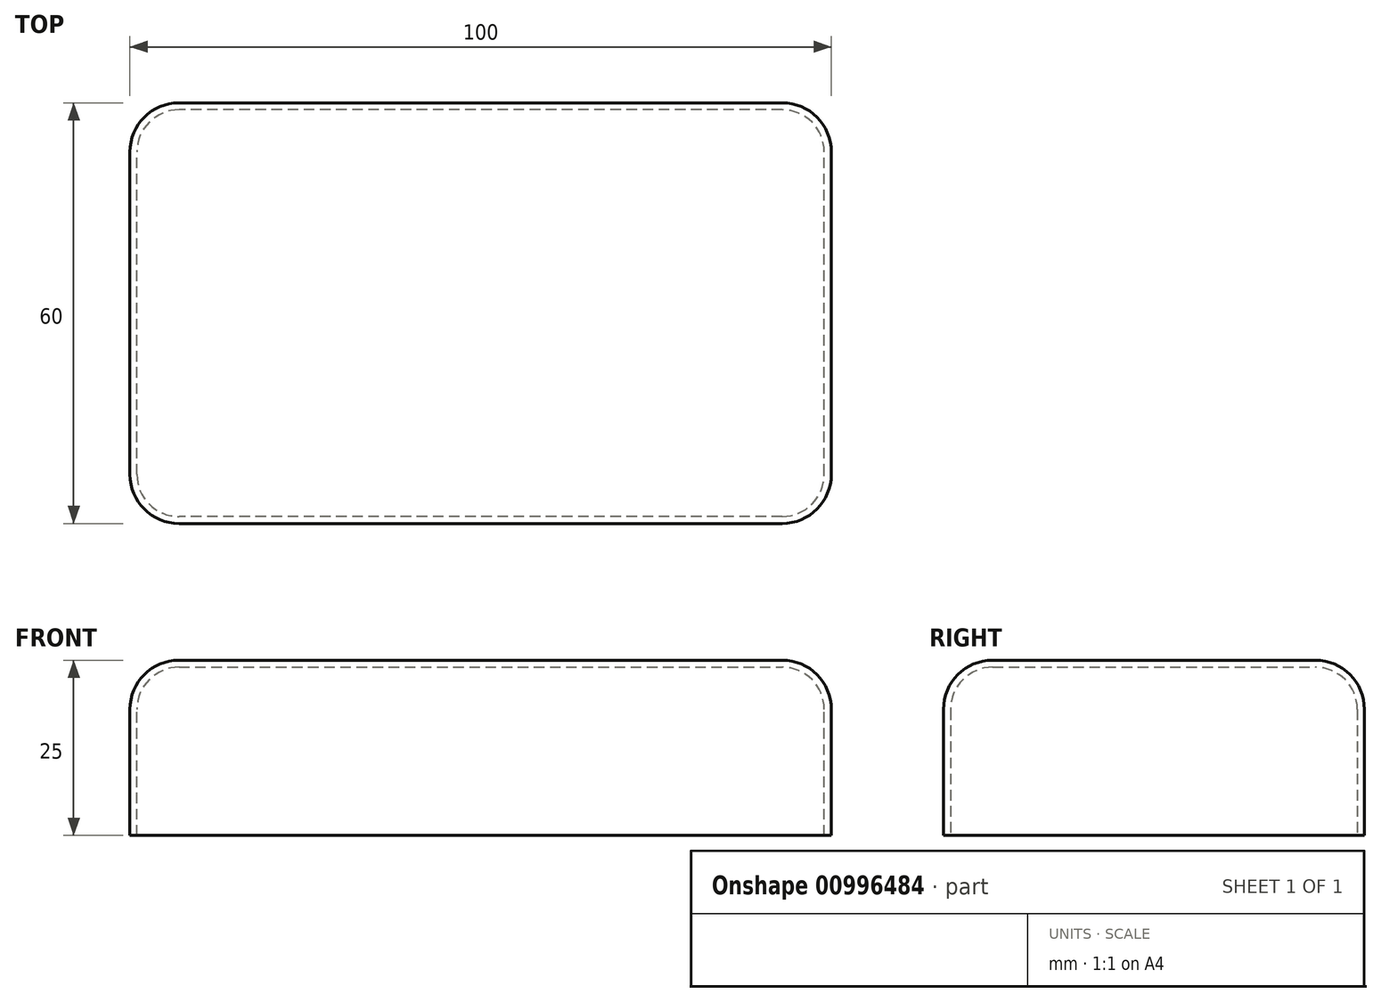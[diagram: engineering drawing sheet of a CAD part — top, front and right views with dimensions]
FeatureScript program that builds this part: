
annotation { "Feature Type Name" : "Feature", "Feature Type Description" : "" }
export const myFeature = defineFeature(function(context is Context, id is Id, definition is map)
    precondition{}
    {
        {
            var Q0;
            Q0=qCreatedBy(makeId("Top.planeOp"),FACE);
            var sketch = newSketch(context, id + "F0", { "sketchPlane" : qUnion([Q0])});
            skLineSegment(sketch, "E0.bottom", {"start": v(50, -30) * mm, "end": v(-50, -30) * mm});
            skLineSegment(sketch, "E0.top", {"start": v(50, 30) * mm, "end": v(-50, 30) * mm});
            skLineSegment(sketch, "E0.left", {"start": v(50, -30) * mm, "end": v(50, 30) * mm});
            skLineSegment(sketch, "E0.right", {"start": v(-50, -30) * mm, "end": v(-50, 30) * mm});
            skPoint(sketch, "E0.middle", {"position": v(0, 0) * mm});
            skSolve(sketch);
        }
        {
            var Q0;
            Q0=makeQuery(id+"F0.imprint","IMPRINT",FACE,{"disambiguationData":[TD([[makeQuery(id+"F0.imprint","IMPRINT",EDGE,{"derivedFrom":sQuery(id+"F0.wireOp",EDGE,"E0.bottom")}),-1.0]])]});
            extrude(context, id + "F1", {"entities" : qUnion([Q0]), "depth" : 25 * mm, "offsetDistance" : 25.4 * mm});
        }
        {
            var Q0;
            Q0=makeQuery(id+"F1.opExtrude","CAP_EDGE",EDGE,{"disambiguationData":[OSD([sQuery(id+"F0.wireOp",EDGE,"E0.bottom")])],"isStart":false});
            var Q1;
            Q1=makeQuery(id+"F1.opExtrude","CAP_EDGE",EDGE,{"disambiguationData":[OSD([sQuery(id+"F0.wireOp",EDGE,"E0.right")])],"isStart":false});
            var Q2;
            Q2=makeQuery(id+"F1.opExtrude","SWEPT_EDGE",EDGE,{"disambiguationData":[OSD([sQuery(id+"F0.wireOp",EDGE,"E0.bottom"),sQuery(id+"F0.wireOp",EDGE,"E0.right")])]});
            var Q3;
            Q3=makeQuery(id+"F1.opExtrude","SWEPT_EDGE",EDGE,{"disambiguationData":[OSD([sQuery(id+"F0.wireOp",EDGE,"E0.top"),sQuery(id+"F0.wireOp",EDGE,"E0.right")])]});
            var Q4;
            Q4=makeQuery(id+"F1.opExtrude","CAP_EDGE",EDGE,{"disambiguationData":[OSD([sQuery(id+"F0.wireOp",EDGE,"E0.top")])],"isStart":false});
            var Q5;
            Q5=makeQuery(id+"F1.opExtrude","SWEPT_EDGE",EDGE,{"disambiguationData":[OSD([sQuery(id+"F0.wireOp",EDGE,"E0.top"),sQuery(id+"F0.wireOp",EDGE,"E0.left")])]});
            var Q6;
            Q6=makeQuery(id+"F1.opExtrude","CAP_EDGE",EDGE,{"disambiguationData":[OSD([sQuery(id+"F0.wireOp",EDGE,"E0.left")])],"isStart":false});
            var Q7;
            Q7=makeQuery(id+"F1.opExtrude","SWEPT_EDGE",EDGE,{"disambiguationData":[OSD([sQuery(id+"F0.wireOp",EDGE,"E0.bottom"),sQuery(id+"F0.wireOp",EDGE,"E0.left")])]});
            fillet(context, id + "F2", {"entities" : qUnion([Q0, Q1, Q2, Q3, Q4, Q5, Q6, Q7]), "radius" : 7 * mm, "tangentPropagation" : true, "allowEdgeOverflow" : false});
        }
        {
            var Q0;
            Q0=makeQuery(id+"F1.opExtrude","CAP_FACE",FACE,{"disambiguationData":[OSD([sQuery(id+"F0.wireOp",EDGE,"E0.bottom"),sQuery(id+"F0.wireOp",EDGE,"E0.top"),sQuery(id+"F0.wireOp",EDGE,"E0.left"),sQuery(id+"F0.wireOp",EDGE,"E0.right")])],"isStart":true});
            shell(context, id + "F3", {"entities" : qUnion([Q0]), "thickness" : 1 * mm});
        }
    });
